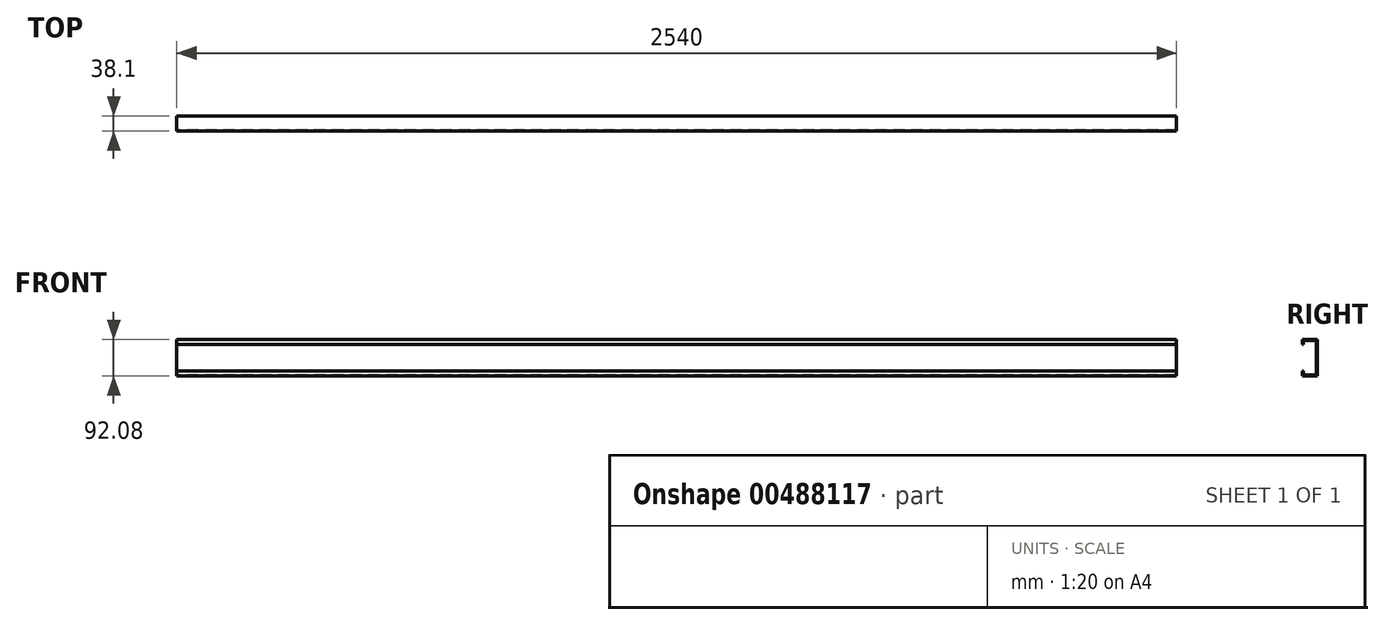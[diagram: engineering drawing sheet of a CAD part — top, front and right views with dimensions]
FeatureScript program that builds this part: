
annotation { "Feature Type Name" : "Feature", "Feature Type Description" : "" }
export const myFeature = defineFeature(function(context is Context, id is Id, definition is map)
    precondition{}
    {
        {
            var Q0;
            Q0=qCreatedBy(makeId("Right.planeOp"),FACE);
            var sketch = newSketch(context, id + "F0", { "sketchPlane" : qUnion([Q0])});
            skLineSegment(sketch, "E0", {"start": v(-19.05, 33.34) * mm, "end": v(-19.05, 46.04) * mm});
            skLineSegment(sketch, "E1", {"start": v(-19.05, 46.04) * mm, "end": v(19.05, 46.04) * mm});
            skLineSegment(sketch, "E2", {"start": v(19.05, 46.04) * mm, "end": v(19.05, -46.04) * mm});
            skLineSegment(sketch, "E3", {"start": v(19.05, -46.04) * mm, "end": v(-19.05, -46.04) * mm});
            skLineSegment(sketch, "E4", {"start": v(-19.05, -46.04) * mm, "end": v(-19.05, -33.34) * mm});
            skLineSegment(sketch, "E5.0", {"start": v(-16.51, -43.5) * mm, "end": v(-16.51, -33.34) * mm});
            skLineSegment(sketch, "E5.1", {"start": v(-16.51, 33.34) * mm, "end": v(-16.51, 43.5) * mm});
            skLineSegment(sketch, "E5.2", {"start": v(-16.51, 43.5) * mm, "end": v(16.51, 43.5) * mm});
            skLineSegment(sketch, "E5.3", {"start": v(16.51, 43.5) * mm, "end": v(16.5, -43.5) * mm});
            skLineSegment(sketch, "E5.4", {"start": v(16.51, -43.5) * mm, "end": v(-16.51, -43.5) * mm});
            skLineSegment(sketch, "E6", {"start": v(-19.05, 33.34) * mm, "end": v(-16.51, 33.34) * mm});
            skLineSegment(sketch, "E7", {"start": v(-19.05, -33.34) * mm, "end": v(-16.51, -33.34) * mm});
            skSolve(sketch);
        }
        {
            var Q0;
            Q0=makeQuery(id+"F0.imprint","IMPRINT",FACE,{"disambiguationData":[TD([[makeQuery(id+"F0.imprint","IMPRINT",EDGE,{"derivedFrom":sQuery(id+"F0.wireOp",EDGE,"E0")}),-1.0]])]});
            extrude(context, id + "F1", {"entities" : qUnion([Q0]), "depth" : 2540 * mm, "offsetDistance" : 25.4 * mm});
        }
    });
